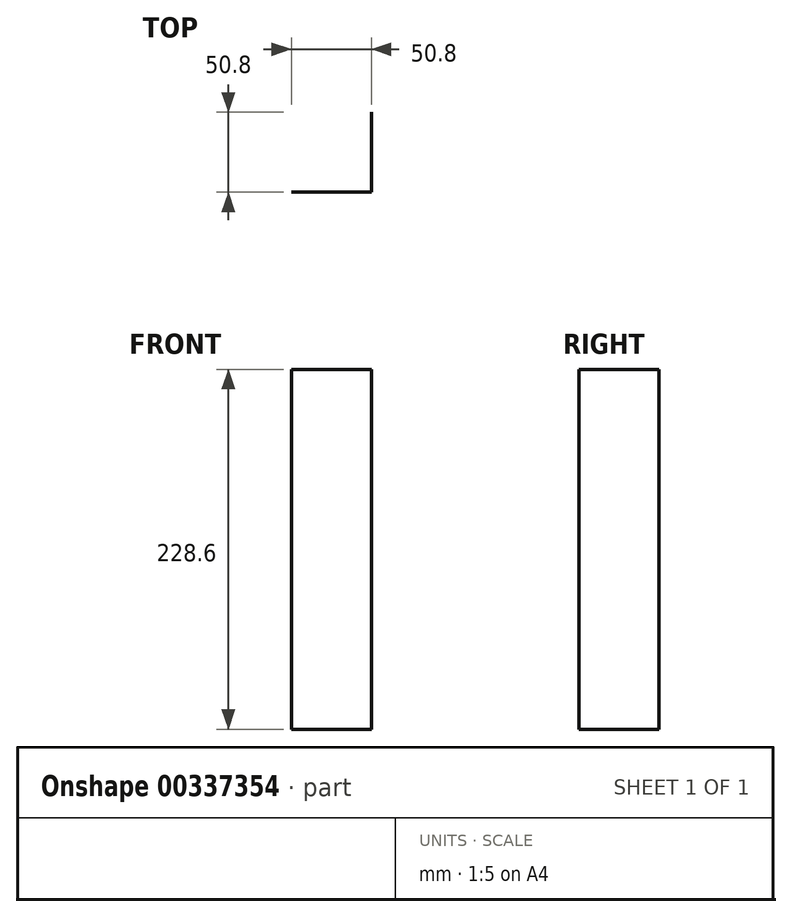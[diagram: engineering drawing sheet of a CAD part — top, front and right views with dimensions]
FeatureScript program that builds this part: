
annotation { "Feature Type Name" : "Feature", "Feature Type Description" : "" }
export const myFeature = defineFeature(function(context is Context, id is Id, definition is map)
    precondition{}
    {
        {
            var Q0;
            Q0=qCreatedBy(makeId("Top.planeOp"),FACE);
            var sketch = newSketch(context, id + "F0", { "sketchPlane" : qUnion([Q0])});
            skLineSegment(sketch, "E0", {"start": v(-49.91, -15.66) * mm, "end": v(0.89, -15.66) * mm});
            skLineSegment(sketch, "E1", {"start": v(0.89, -15.66) * mm, "end": v(0.89, 35.14) * mm});
            skSolve(sketch);
        }
        {
            var Q0;
            Q0=sQuery(id+"F0.wireOp",EDGE,"E0");
            var Q1;
            Q1=sQuery(id+"F0.wireOp",EDGE,"E1");
            extrude(context, id + "F1", {"bodyType" : ToolBodyType.SURFACE, "surfaceEntities" : qUnion([Q0, Q1]), "depth" : 228.6 * mm});
        }
    });
